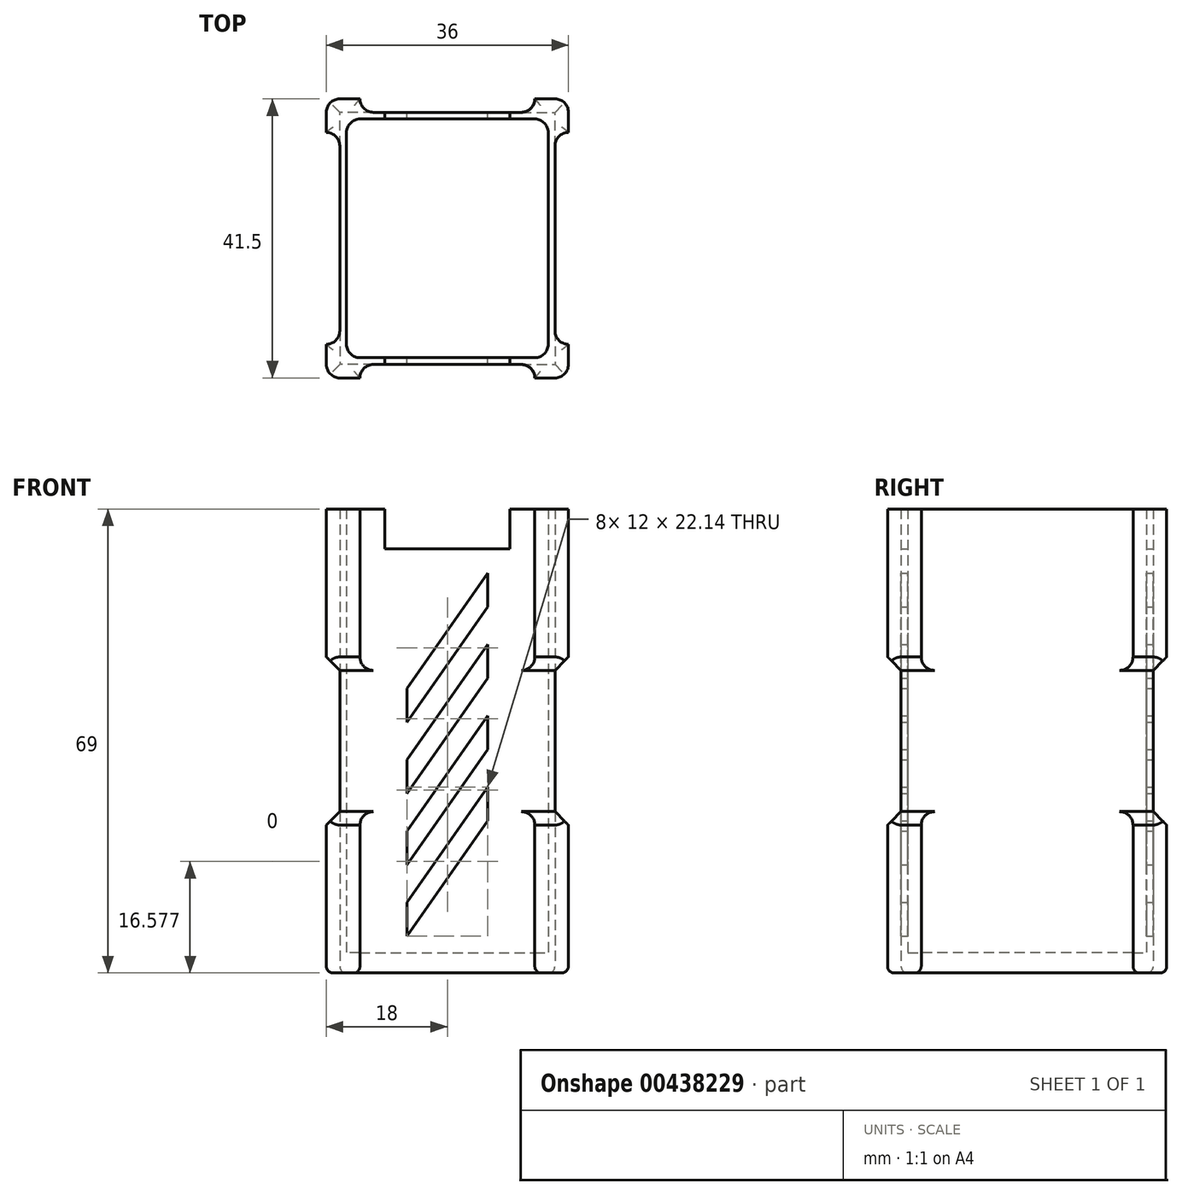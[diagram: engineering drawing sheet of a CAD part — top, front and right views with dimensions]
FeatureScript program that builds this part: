
annotation { "Feature Type Name" : "Feature", "Feature Type Description" : "" }
export const myFeature = defineFeature(function(context is Context, id is Id, definition is map)
    precondition{}
    {
        {
            var Q0;
            Q0=qCreatedBy(makeId("Top.planeOp"),FACE);
            var sketch = newSketch(context, id + "F0", { "sketchPlane" : qUnion([Q0])});
            skLineSegment(sketch, "E0.bottom", {"start": v(-15, 17.75) * mm, "end": v(15, 17.75) * mm});
            skLineSegment(sketch, "E0.top", {"start": v(-15, -17.75) * mm, "end": v(15, -17.75) * mm});
            skLineSegment(sketch, "E0.left", {"start": v(-15, 17.75) * mm, "end": v(-15, -17.75) * mm});
            skLineSegment(sketch, "E0.right", {"start": v(15, 17.75) * mm, "end": v(15, -17.75) * mm});
            skPoint(sketch, "E0.middle", {"position": v(0, 0) * mm});
            skLineSegment(sketch, "E1.0", {"start": v(-16, 18.75) * mm, "end": v(16, 18.75) * mm});
            skLineSegment(sketch, "E1.1", {"start": v(-16, 18.75) * mm, "end": v(-16, -18.75) * mm});
            skLineSegment(sketch, "E1.2", {"start": v(-16, -18.75) * mm, "end": v(16, -18.75) * mm});
            skLineSegment(sketch, "E1.3", {"start": v(16, 18.75) * mm, "end": v(16, -18.75) * mm});
            skLineSegment(sketch, "E2.0", {"start": v(18, 20.75) * mm, "end": v(18, 15.75) * mm});
            skLineSegment(sketch, "E2.1", {"start": v(-18, 20.75) * mm, "end": v(-13, 20.75) * mm});
            skLineSegment(sketch, "E2.2", {"start": v(-18, 20.75) * mm, "end": v(-18, 15.75) * mm});
            skLineSegment(sketch, "E2.3", {"start": v(-18, -20.75) * mm, "end": v(-13, -20.75) * mm});
            skLineSegment(sketch, "E3", {"start": v(-18, 15.75) * mm, "end": v(-16, 15.75) * mm});
            skLineSegment(sketch, "E4", {"start": v(-13, 20.75) * mm, "end": v(-13, 18.75) * mm});
            skLineSegment(sketch, "E5", {"start": v(13, 20.75) * mm, "end": v(13, 18.75) * mm});
            skLineSegment(sketch, "E6", {"start": v(18, -15.75) * mm, "end": v(16, -15.75) * mm});
            skLineSegment(sketch, "E7.trimOffspring", {"start": v(-18, -15.75) * mm, "end": v(-18, -20.75) * mm});
            skLineSegment(sketch, "E8.trimOffspring", {"start": v(13, 20.75) * mm, "end": v(18, 20.75) * mm});
            skLineSegment(sketch, "E9.trimOffspring", {"start": v(18, -15.75) * mm, "end": v(18, -20.75) * mm});
            skLineSegment(sketch, "E10.trimOffspring", {"start": v(13, -20.75) * mm, "end": v(18, -20.75) * mm});
            skLineSegment(sketch, "E11.trimOffspring", {"start": v(16, 15.75) * mm, "end": v(18, 15.75) * mm});
            skLineSegment(sketch, "E12.trimOffspring", {"start": v(-13, -18.75) * mm, "end": v(-13, -20.75) * mm});
            skLineSegment(sketch, "E13.trimOffspring", {"start": v(-16, -15.75) * mm, "end": v(-18, -15.75) * mm});
            skLineSegment(sketch, "E14.trimOffspring", {"start": v(13, -18.75) * mm, "end": v(13, -20.75) * mm});
            skSolve(sketch);
        }
        {
            var Q0;
            Q0 = qSketchRegion(id + "F0", true);
            extrude(context, id + "F1", {"entities" : qUnion([Q0]), "depth" : 66 * mm});
        }
        {
            var Q0;
            Q0=makeQuery(id+"F0.imprint","IMPRINT",FACE,{"disambiguationData":[TD([[makeQuery(id+"F0.imprint","IMPRINT",EDGE,{"derivedFrom":sQuery(id+"F0.wireOp",EDGE,"E0.bottom")}),1.0]])]});
            var Q1;
            Q1=makeQuery(id+"F0.imprint","IMPRINT",FACE,{"disambiguationData":[TD([[makeQuery(id+"F0.imprint","IMPRINT",EDGE,{"derivedFrom":sQuery(id+"F0.wireOp",EDGE,"E0.bottom")}),-1.0]])]});
            var Q2;
            {var subQ3=sQuery(id+"F0.wireOp",EDGE,"E6");Q2=makeQuery(id+"F0.imprint","IMPRINT",FACE,{"disambiguationData":[TD([[makeQuery(id+"F0.imprint","IMPRINT",EDGE,{"derivedFrom":subQ3}),1.0]])]});}
            var Q3;
            Q3=makeQuery(id+"F0.imprint","IMPRINT",FACE,{"disambiguationData":[TD([[makeQuery(id+"F0.imprint","IMPRINT",EDGE,{"derivedFrom":sQuery(id+"F0.wireOp",EDGE,"E2.3")}),1.0]])]});
            var Q4;
            Q4=makeQuery(id+"F0.imprint","IMPRINT",FACE,{"disambiguationData":[TD([[makeQuery(id+"F0.imprint","IMPRINT",EDGE,{"derivedFrom":sQuery(id+"F0.wireOp",EDGE,"E2.0")}),-1.0]])]});
            var Q5;
            Q5=makeQuery(id+"F0.imprint","IMPRINT",FACE,{"disambiguationData":[TD([[makeQuery(id+"F0.imprint","IMPRINT",EDGE,{"derivedFrom":sQuery(id+"F0.wireOp",EDGE,"E2.1")}),-1.0]])]});
            extrude(context, id + "F2", {"entities" : qUnion([Q0, Q1, Q2, Q3, Q4, Q5]), "operationType" : NewBodyOperationType.ADD, "oppositeDirection" : true, "depth" : 3 * mm});
        }
        {
            var Q0;
            {var subQ0=sQuery(id+"F0.wireOp",EDGE,"E13.trimOffspring");var subQ1=sQuery(id+"F0.wireOp",EDGE,"E1.1");Q0=makeQuery(id+"F2.boolean.opBoolean","MERGE",EDGE,{"derivedFrom":[makeQuery(id+"F1.opExtrude","SWEPT_EDGE",EDGE,{"disambiguationData":[OSD([subQ1,subQ0])]}),makeQuery(id+"F2.opExtrude","SWEPT_EDGE",EDGE,{"disambiguationData":[OSD([subQ1,subQ0])]})]});}
            var Q1;
            {var subQ0=sQuery(id+"F0.wireOp",EDGE,"E3");var subQ1=sQuery(id+"F0.wireOp",EDGE,"E1.1");Q1=makeQuery(id+"F2.boolean.opBoolean","MERGE",EDGE,{"derivedFrom":[makeQuery(id+"F1.opExtrude","SWEPT_EDGE",EDGE,{"disambiguationData":[OSD([subQ1,subQ0])]}),makeQuery(id+"F2.opExtrude","SWEPT_EDGE",EDGE,{"disambiguationData":[OSD([subQ1,subQ0])]})]});}
            var Q2;
            {var subQ0=sQuery(id+"F0.wireOp",EDGE,"E4");var subQ1=sQuery(id+"F0.wireOp",EDGE,"E1.0");Q2=makeQuery(id+"F2.boolean.opBoolean","MERGE",EDGE,{"derivedFrom":[makeQuery(id+"F1.opExtrude","SWEPT_EDGE",EDGE,{"disambiguationData":[OSD([subQ1,subQ0])]}),makeQuery(id+"F2.opExtrude","SWEPT_EDGE",EDGE,{"disambiguationData":[OSD([subQ1,subQ0])]})]});}
            var Q3;
            {var subQ0=sQuery(id+"F0.wireOp",EDGE,"E5");var subQ1=sQuery(id+"F0.wireOp",EDGE,"E1.0");Q3=makeQuery(id+"F2.boolean.opBoolean","MERGE",EDGE,{"derivedFrom":[makeQuery(id+"F1.opExtrude","SWEPT_EDGE",EDGE,{"disambiguationData":[OSD([subQ1,subQ0])]}),makeQuery(id+"F2.opExtrude","SWEPT_EDGE",EDGE,{"disambiguationData":[OSD([subQ1,subQ0])]})]});}
            var Q4;
            {var subQ0=sQuery(id+"F0.wireOp",EDGE,"E11.trimOffspring");var subQ1=sQuery(id+"F0.wireOp",EDGE,"E1.3");Q4=makeQuery(id+"F2.boolean.opBoolean","MERGE",EDGE,{"derivedFrom":[makeQuery(id+"F1.opExtrude","SWEPT_EDGE",EDGE,{"disambiguationData":[OSD([subQ1,subQ0])]}),makeQuery(id+"F2.opExtrude","SWEPT_EDGE",EDGE,{"disambiguationData":[OSD([subQ1,subQ0])]})]});}
            var Q5;
            {var subQ0=sQuery(id+"F0.wireOp",EDGE,"E14.trimOffspring");var subQ1=sQuery(id+"F0.wireOp",EDGE,"E1.2");Q5=makeQuery(id+"F2.boolean.opBoolean","MERGE",EDGE,{"derivedFrom":[makeQuery(id+"F1.opExtrude","SWEPT_EDGE",EDGE,{"disambiguationData":[OSD([subQ1,subQ0])]}),makeQuery(id+"F2.opExtrude","SWEPT_EDGE",EDGE,{"disambiguationData":[OSD([subQ1,subQ0])]})]});}
            var Q6;
            {var subQ0=sQuery(id+"F0.wireOp",EDGE,"E6");var subQ1=sQuery(id+"F0.wireOp",EDGE,"E1.3");Q6=makeQuery(id+"F2.boolean.opBoolean","MERGE",EDGE,{"derivedFrom":[makeQuery(id+"F1.opExtrude","SWEPT_EDGE",EDGE,{"disambiguationData":[OSD([subQ1,subQ0])]}),makeQuery(id+"F2.opExtrude","SWEPT_EDGE",EDGE,{"disambiguationData":[OSD([subQ1,subQ0])]})]});}
            var Q7;
            {var subQ0=sQuery(id+"F0.wireOp",EDGE,"E12.trimOffspring");var subQ1=sQuery(id+"F0.wireOp",EDGE,"E1.2");Q7=makeQuery(id+"F2.boolean.opBoolean","MERGE",EDGE,{"derivedFrom":[makeQuery(id+"F1.opExtrude","SWEPT_EDGE",EDGE,{"disambiguationData":[OSD([subQ1,subQ0])]}),makeQuery(id+"F2.opExtrude","SWEPT_EDGE",EDGE,{"disambiguationData":[OSD([subQ1,subQ0])]})]});}
            fillet(context, id + "F3", {"entities" : qUnion([Q0, Q1, Q2, Q3, Q4, Q5, Q6, Q7]), "radius" : 2 * mm, "tangentPropagation" : true, "allowEdgeOverflow" : false});
        }
        {
            var Q0;
            {var subQ0=sQuery(id+"F0.wireOp",EDGE,"E8.trimOffspring");var subQ1=sQuery(id+"F0.wireOp",EDGE,"E2.0");Q0=makeQuery(id+"F2.boolean.opBoolean","MERGE",EDGE,{"derivedFrom":[makeQuery(id+"F1.opExtrude","SWEPT_EDGE",EDGE,{"disambiguationData":[OSD([subQ1,subQ0])]}),makeQuery(id+"F2.opExtrude","SWEPT_EDGE",EDGE,{"disambiguationData":[OSD([subQ1,subQ0])]})]});}
            var Q1;
            {var subQ0=sQuery(id+"F0.wireOp",EDGE,"E7.trimOffspring");var subQ1=sQuery(id+"F0.wireOp",EDGE,"E2.3");Q1=makeQuery(id+"F2.boolean.opBoolean","MERGE",EDGE,{"derivedFrom":[makeQuery(id+"F1.opExtrude","SWEPT_EDGE",EDGE,{"disambiguationData":[OSD([subQ1,subQ0])]}),makeQuery(id+"F2.opExtrude","SWEPT_EDGE",EDGE,{"disambiguationData":[OSD([subQ1,subQ0])]})]});}
            var Q2;
            {var subQ0=sQuery(id+"F0.wireOp",EDGE,"E2.2");var subQ1=sQuery(id+"F0.wireOp",EDGE,"E2.1");Q2=makeQuery(id+"F2.boolean.opBoolean","MERGE",EDGE,{"derivedFrom":[makeQuery(id+"F1.opExtrude","SWEPT_EDGE",EDGE,{"disambiguationData":[OSD([subQ1,subQ0])]}),makeQuery(id+"F2.opExtrude","SWEPT_EDGE",EDGE,{"disambiguationData":[OSD([subQ1,subQ0])]})]});}
            var Q3;
            {var subQ0=sQuery(id+"F0.wireOp",EDGE,"E10.trimOffspring");var subQ1=sQuery(id+"F0.wireOp",EDGE,"E9.trimOffspring");Q3=makeQuery(id+"F2.boolean.opBoolean","MERGE",EDGE,{"derivedFrom":[makeQuery(id+"F1.opExtrude","SWEPT_EDGE",EDGE,{"disambiguationData":[OSD([subQ1,subQ0])]}),makeQuery(id+"F2.opExtrude","SWEPT_EDGE",EDGE,{"disambiguationData":[OSD([subQ1,subQ0])]})]});}
            fillet(context, id + "F4", {"entities" : qUnion([Q0, Q1, Q2, Q3]), "radius" : 2 * mm, "tangentPropagation" : true, "allowEdgeOverflow" : false});
        }
        {
            var Q0;
            Q0=makeQuery(id+"F2.opExtrude","CAP_FACE",FACE,{"disambiguationData":[OSD([sQuery(id+"F0.wireOp",EDGE,"E1.0"),sQuery(id+"F0.wireOp",EDGE,"E1.1"),sQuery(id+"F0.wireOp",EDGE,"E1.2"),sQuery(id+"F0.wireOp",EDGE,"E1.3"),sQuery(id+"F0.wireOp",EDGE,"E2.0"),sQuery(id+"F0.wireOp",EDGE,"E2.1"),sQuery(id+"F0.wireOp",EDGE,"E2.2"),sQuery(id+"F0.wireOp",EDGE,"E2.3"),sQuery(id+"F0.wireOp",EDGE,"E3"),sQuery(id+"F0.wireOp",EDGE,"E4"),sQuery(id+"F0.wireOp",EDGE,"E5"),sQuery(id+"F0.wireOp",EDGE,"E6"),sQuery(id+"F0.wireOp",EDGE,"E7.trimOffspring"),sQuery(id+"F0.wireOp",EDGE,"E8.trimOffspring"),sQuery(id+"F0.wireOp",EDGE,"E9.trimOffspring"),sQuery(id+"F0.wireOp",EDGE,"E10.trimOffspring"),sQuery(id+"F0.wireOp",EDGE,"E11.trimOffspring"),sQuery(id+"F0.wireOp",EDGE,"E12.trimOffspring"),sQuery(id+"F0.wireOp",EDGE,"E13.trimOffspring"),sQuery(id+"F0.wireOp",EDGE,"E14.trimOffspring")])],"isStart":false});
            var Q1;
            Q1=makeQuery(id+"F1.opExtrude","CAP_FACE",FACE,{"disambiguationData":[OSD([sQuery(id+"F0.wireOp",EDGE,"E0.bottom"),sQuery(id+"F0.wireOp",EDGE,"E0.top"),sQuery(id+"F0.wireOp",EDGE,"E0.left"),sQuery(id+"F0.wireOp",EDGE,"E0.right"),sQuery(id+"F0.wireOp",EDGE,"E1.0"),sQuery(id+"F0.wireOp",EDGE,"E1.1"),sQuery(id+"F0.wireOp",EDGE,"E1.2"),sQuery(id+"F0.wireOp",EDGE,"E1.3"),sQuery(id+"F0.wireOp",EDGE,"E2.0"),sQuery(id+"F0.wireOp",EDGE,"E2.1"),sQuery(id+"F0.wireOp",EDGE,"E2.2"),sQuery(id+"F0.wireOp",EDGE,"E2.3"),sQuery(id+"F0.wireOp",EDGE,"E3"),sQuery(id+"F0.wireOp",EDGE,"E4"),sQuery(id+"F0.wireOp",EDGE,"E5"),sQuery(id+"F0.wireOp",EDGE,"E6"),sQuery(id+"F0.wireOp",EDGE,"E7.trimOffspring"),sQuery(id+"F0.wireOp",EDGE,"E8.trimOffspring"),sQuery(id+"F0.wireOp",EDGE,"E9.trimOffspring"),sQuery(id+"F0.wireOp",EDGE,"E10.trimOffspring"),sQuery(id+"F0.wireOp",EDGE,"E11.trimOffspring"),sQuery(id+"F0.wireOp",EDGE,"E12.trimOffspring"),sQuery(id+"F0.wireOp",EDGE,"E13.trimOffspring"),sQuery(id+"F0.wireOp",EDGE,"E14.trimOffspring")])],"isStart":false});
            cPlane(context, id + "F5", {"entities" : qUnion([Q0, Q1]), "cplaneType" : CPlaneType.MID_PLANE, "offset" : 25 * mm, "width" : 150 * mm, "height" : 150 * mm});
        }
        {
            var Q0;
            Q0=qCreatedBy(id+"F5.planeOp",FACE);
            var sketch = newSketch(context, id + "F6", { "sketchPlane" : qUnion([Q0])});
            skLineSegment(sketch, "E15.bottom", {"start": v(18, 20.75) * mm, "end": v(-18, 20.75) * mm});
            skLineSegment(sketch, "E15.top", {"start": v(18, -20.75) * mm, "end": v(-18, -20.75) * mm});
            skLineSegment(sketch, "E15.left", {"start": v(18, 20.75) * mm, "end": v(18, -20.75) * mm});
            skLineSegment(sketch, "E15.right", {"start": v(-18, 20.75) * mm, "end": v(-18, -20.75) * mm});
            skLineSegment(sketch, "E16.0", {"start": v(16, -18.75) * mm, "end": v(-16, -18.75) * mm});
            skLineSegment(sketch, "E16.1", {"start": v(16, 18.75) * mm, "end": v(16, -18.75) * mm});
            skLineSegment(sketch, "E16.2", {"start": v(16, 18.75) * mm, "end": v(-16, 18.75) * mm});
            skLineSegment(sketch, "E16.3", {"start": v(-16, 18.75) * mm, "end": v(-16, -18.75) * mm});
            skSolve(sketch);
        }
        {
            var Q0;
            Q0 = qSketchRegion(id + "F6", true);
            extrude(context, id + "F7", {"entities" : qUnion([Q0]), "operationType" : NewBodyOperationType.REMOVE, "endBound" : BoundingType.SYMMETRIC, "oppositeDirection" : true, "depth" : 25 * mm});
        }
        {
            var Q0;
            {var subQ0=sQuery(id+"F0.wireOp",EDGE,"E1.1");var subQ3=sQuery(id+"F6.wireOp",EDGE,"E16.0");Q0=makeQuery(id+"F7.boolean.opBoolean","COPY",EDGE,{"disambiguationData":[TD([makeQuery(id+"F1.opExtrude","SWEPT_FACE",FACE,{"disambiguationData":[OSD([subQ0])]})])],"derivedFrom":makeQuery(id+"F7.opExtrude","CAP_EDGE",EDGE,{"disambiguationData":[OSD([subQ3])],"isStart":true})});}
            var Q1;
            {var subQ1=sQuery(id+"F0.wireOp",EDGE,"E1.0");var subQ2=sQuery(id+"F6.wireOp",EDGE,"E16.3");Q1=makeQuery(id+"F7.boolean.opBoolean","COPY",EDGE,{"disambiguationData":[TD([makeQuery(id+"F1.opExtrude","SWEPT_FACE",FACE,{"disambiguationData":[OSD([subQ1])]})])],"derivedFrom":makeQuery(id+"F7.opExtrude","CAP_EDGE",EDGE,{"disambiguationData":[OSD([subQ2])],"isStart":true})});}
            var Q2;
            {var subQ0=sQuery(id+"F0.wireOp",EDGE,"E1.3");var subQ3=sQuery(id+"F6.wireOp",EDGE,"E16.0");Q2=makeQuery(id+"F7.boolean.opBoolean","COPY",EDGE,{"disambiguationData":[TD([makeQuery(id+"F1.opExtrude","SWEPT_FACE",FACE,{"disambiguationData":[OSD([subQ0])]})])],"derivedFrom":makeQuery(id+"F7.opExtrude","CAP_EDGE",EDGE,{"disambiguationData":[OSD([subQ3])],"isStart":true})});}
            var Q3;
            {var subQ1=sQuery(id+"F0.wireOp",EDGE,"E1.0");var subQ2=sQuery(id+"F6.wireOp",EDGE,"E16.1");Q3=makeQuery(id+"F7.boolean.opBoolean","COPY",EDGE,{"disambiguationData":[TD([makeQuery(id+"F1.opExtrude","SWEPT_FACE",FACE,{"disambiguationData":[OSD([subQ1])]})])],"derivedFrom":makeQuery(id+"F7.opExtrude","CAP_EDGE",EDGE,{"disambiguationData":[OSD([subQ2])],"isStart":true})});}
            var Q4;
            {var subQ0=sQuery(id+"F0.wireOp",EDGE,"E1.1");var subQ3=sQuery(id+"F6.wireOp",EDGE,"E16.0");Q4=makeQuery(id+"F7.boolean.opBoolean","COPY",EDGE,{"disambiguationData":[TD([makeQuery(id+"F1.opExtrude","SWEPT_FACE",FACE,{"disambiguationData":[OSD([subQ0])]})])],"derivedFrom":makeQuery(id+"F7.opExtrude","CAP_EDGE",EDGE,{"disambiguationData":[OSD([subQ3])],"isStart":false})});}
            var Q5;
            {var subQ1=sQuery(id+"F0.wireOp",EDGE,"E1.0");var subQ2=sQuery(id+"F6.wireOp",EDGE,"E16.3");Q5=makeQuery(id+"F7.boolean.opBoolean","COPY",EDGE,{"disambiguationData":[TD([makeQuery(id+"F1.opExtrude","SWEPT_FACE",FACE,{"disambiguationData":[OSD([subQ1])]})])],"derivedFrom":makeQuery(id+"F7.opExtrude","CAP_EDGE",EDGE,{"disambiguationData":[OSD([subQ2])],"isStart":false})});}
            var Q6;
            {var subQ0=sQuery(id+"F0.wireOp",EDGE,"E1.3");var subQ2=sQuery(id+"F6.wireOp",EDGE,"E16.2");Q6=makeQuery(id+"F7.boolean.opBoolean","COPY",EDGE,{"disambiguationData":[TD([makeQuery(id+"F1.opExtrude","SWEPT_FACE",FACE,{"disambiguationData":[OSD([subQ0])]})])],"derivedFrom":makeQuery(id+"F7.opExtrude","CAP_EDGE",EDGE,{"disambiguationData":[OSD([subQ2])],"isStart":false})});}
            var Q7;
            {var subQ0=sQuery(id+"F0.wireOp",EDGE,"E1.3");var subQ3=sQuery(id+"F6.wireOp",EDGE,"E16.0");Q7=makeQuery(id+"F7.boolean.opBoolean","COPY",EDGE,{"disambiguationData":[TD([makeQuery(id+"F1.opExtrude","SWEPT_FACE",FACE,{"disambiguationData":[OSD([subQ0])]})])],"derivedFrom":makeQuery(id+"F7.opExtrude","CAP_EDGE",EDGE,{"disambiguationData":[OSD([subQ3])],"isStart":false})});}
            var Q8;
            {var subQ1=sQuery(id+"F0.wireOp",EDGE,"E1.2");var subQ3=sQuery(id+"F6.wireOp",EDGE,"E16.1");Q8=makeQuery(id+"F7.boolean.opBoolean","COPY",EDGE,{"disambiguationData":[TD([makeQuery(id+"F1.opExtrude","SWEPT_FACE",FACE,{"disambiguationData":[OSD([subQ1])]})])],"derivedFrom":makeQuery(id+"F7.opExtrude","CAP_EDGE",EDGE,{"disambiguationData":[OSD([subQ3])],"isStart":true})});}
            var Q9;
            {var subQ1=sQuery(id+"F0.wireOp",EDGE,"E1.0");var subQ2=sQuery(id+"F6.wireOp",EDGE,"E16.1");Q9=makeQuery(id+"F7.boolean.opBoolean","COPY",EDGE,{"disambiguationData":[TD([makeQuery(id+"F1.opExtrude","SWEPT_FACE",FACE,{"disambiguationData":[OSD([subQ1])]})])],"derivedFrom":makeQuery(id+"F7.opExtrude","CAP_EDGE",EDGE,{"disambiguationData":[OSD([subQ2])],"isStart":false})});}
            var Q10;
            {var subQ1=sQuery(id+"F0.wireOp",EDGE,"E1.2");var subQ3=sQuery(id+"F6.wireOp",EDGE,"E16.1");Q10=makeQuery(id+"F7.boolean.opBoolean","COPY",EDGE,{"disambiguationData":[TD([makeQuery(id+"F1.opExtrude","SWEPT_FACE",FACE,{"disambiguationData":[OSD([subQ1])]})])],"derivedFrom":makeQuery(id+"F7.opExtrude","CAP_EDGE",EDGE,{"disambiguationData":[OSD([subQ3])],"isStart":false})});}
            var Q11;
            {var subQ2=sQuery(id+"F0.wireOp",EDGE,"E1.1");var subQ3=sQuery(id+"F6.wireOp",EDGE,"E16.2");Q11=makeQuery(id+"F7.boolean.opBoolean","COPY",EDGE,{"disambiguationData":[TD([makeQuery(id+"F1.opExtrude","SWEPT_FACE",FACE,{"disambiguationData":[OSD([subQ2])]})])],"derivedFrom":makeQuery(id+"F7.opExtrude","CAP_EDGE",EDGE,{"disambiguationData":[OSD([subQ3])],"isStart":false})});}
            var Q12;
            {var subQ0=sQuery(id+"F0.wireOp",EDGE,"E1.2");var subQ1=sQuery(id+"F6.wireOp",EDGE,"E16.3");Q12=makeQuery(id+"F7.boolean.opBoolean","COPY",EDGE,{"disambiguationData":[TD([makeQuery(id+"F1.opExtrude","SWEPT_FACE",FACE,{"disambiguationData":[OSD([subQ0])]})])],"derivedFrom":makeQuery(id+"F7.opExtrude","CAP_EDGE",EDGE,{"disambiguationData":[OSD([subQ1])],"isStart":false})});}
            var Q13;
            {var subQ0=sQuery(id+"F0.wireOp",EDGE,"E1.2");var subQ1=sQuery(id+"F6.wireOp",EDGE,"E16.3");Q13=makeQuery(id+"F7.boolean.opBoolean","COPY",EDGE,{"disambiguationData":[TD([makeQuery(id+"F1.opExtrude","SWEPT_FACE",FACE,{"disambiguationData":[OSD([subQ0])]})])],"derivedFrom":makeQuery(id+"F7.opExtrude","CAP_EDGE",EDGE,{"disambiguationData":[OSD([subQ1])],"isStart":true})});}
            var Q14;
            {var subQ2=sQuery(id+"F0.wireOp",EDGE,"E1.1");var subQ3=sQuery(id+"F6.wireOp",EDGE,"E16.2");Q14=makeQuery(id+"F7.boolean.opBoolean","COPY",EDGE,{"disambiguationData":[TD([makeQuery(id+"F1.opExtrude","SWEPT_FACE",FACE,{"disambiguationData":[OSD([subQ2])]})])],"derivedFrom":makeQuery(id+"F7.opExtrude","CAP_EDGE",EDGE,{"disambiguationData":[OSD([subQ3])],"isStart":true})});}
            var Q15;
            {var subQ0=sQuery(id+"F0.wireOp",EDGE,"E1.3");var subQ2=sQuery(id+"F6.wireOp",EDGE,"E16.2");Q15=makeQuery(id+"F7.boolean.opBoolean","COPY",EDGE,{"disambiguationData":[TD([makeQuery(id+"F1.opExtrude","SWEPT_FACE",FACE,{"disambiguationData":[OSD([subQ0])]})])],"derivedFrom":makeQuery(id+"F7.opExtrude","CAP_EDGE",EDGE,{"disambiguationData":[OSD([subQ2])],"isStart":true})});}
            chamfer(context, id + "F8", {"entities" : qUnion([Q0, Q1, Q2, Q3, Q4, Q5, Q6, Q7, Q8, Q9, Q10, Q11, Q12, Q13, Q14, Q15]), "chamferType" : ChamferType.OFFSET_ANGLE, "width" : 2 * mm, "oppositeDirection" : false, "angle" : 45 * degree, "tangentPropagation" : true});
        }
        {
            var Q0;
            Q0=makeQuery(id+"F2.opExtrude","CAP_EDGE",EDGE,{"disambiguationData":[OSD([sQuery(id+"F0.wireOp",EDGE,"E2.2")])],"isStart":false});
            var Q1;
            Q1=makeQuery(id+"F2.opExtrude","CAP_EDGE",EDGE,{"disambiguationData":[OSD([sQuery(id+"F0.wireOp",EDGE,"E1.1")])],"isStart":false});
            var Q2;
            {var subQ0=sQuery(id+"F0.wireOp",EDGE,"E7.trimOffspring");var subQ1=sQuery(id+"F0.wireOp",EDGE,"E2.3");Q2=makeQuery(id+"F4.opFillet","BLEND_EDGE",EDGE,{"blendedFrom":[makeQuery(id+"F2.boolean.opBoolean","MERGE",EDGE,{"derivedFrom":[makeQuery(id+"F1.opExtrude","SWEPT_EDGE",EDGE,{"disambiguationData":[OSD([subQ1,subQ0])]}),makeQuery(id+"F2.opExtrude","SWEPT_EDGE",EDGE,{"disambiguationData":[OSD([subQ1,subQ0])]})]}),makeQuery(id+"F2.opExtrude","CAP_FACE",FACE,{"disambiguationData":[OSD([sQuery(id+"F0.wireOp",EDGE,"E1.0"),sQuery(id+"F0.wireOp",EDGE,"E1.1"),sQuery(id+"F0.wireOp",EDGE,"E1.2"),sQuery(id+"F0.wireOp",EDGE,"E1.3"),sQuery(id+"F0.wireOp",EDGE,"E2.0"),sQuery(id+"F0.wireOp",EDGE,"E2.1"),sQuery(id+"F0.wireOp",EDGE,"E2.2"),subQ1,sQuery(id+"F0.wireOp",EDGE,"E3"),sQuery(id+"F0.wireOp",EDGE,"E4"),sQuery(id+"F0.wireOp",EDGE,"E5"),sQuery(id+"F0.wireOp",EDGE,"E6"),subQ0,sQuery(id+"F0.wireOp",EDGE,"E8.trimOffspring"),sQuery(id+"F0.wireOp",EDGE,"E9.trimOffspring"),sQuery(id+"F0.wireOp",EDGE,"E10.trimOffspring"),sQuery(id+"F0.wireOp",EDGE,"E11.trimOffspring"),sQuery(id+"F0.wireOp",EDGE,"E12.trimOffspring"),sQuery(id+"F0.wireOp",EDGE,"E13.trimOffspring"),sQuery(id+"F0.wireOp",EDGE,"E14.trimOffspring")])],"isStart":false})],"blendedInto":[makeQuery(id+"F2.opExtrude","CAP_FACE",FACE,{"disambiguationData":[OSD([sQuery(id+"F0.wireOp",EDGE,"E1.0"),sQuery(id+"F0.wireOp",EDGE,"E1.1"),sQuery(id+"F0.wireOp",EDGE,"E1.2"),sQuery(id+"F0.wireOp",EDGE,"E1.3"),sQuery(id+"F0.wireOp",EDGE,"E2.0"),sQuery(id+"F0.wireOp",EDGE,"E2.1"),sQuery(id+"F0.wireOp",EDGE,"E2.2"),subQ1,sQuery(id+"F0.wireOp",EDGE,"E3"),sQuery(id+"F0.wireOp",EDGE,"E4"),sQuery(id+"F0.wireOp",EDGE,"E5"),sQuery(id+"F0.wireOp",EDGE,"E6"),subQ0,sQuery(id+"F0.wireOp",EDGE,"E8.trimOffspring"),sQuery(id+"F0.wireOp",EDGE,"E9.trimOffspring"),sQuery(id+"F0.wireOp",EDGE,"E10.trimOffspring"),sQuery(id+"F0.wireOp",EDGE,"E11.trimOffspring"),sQuery(id+"F0.wireOp",EDGE,"E12.trimOffspring"),sQuery(id+"F0.wireOp",EDGE,"E13.trimOffspring"),sQuery(id+"F0.wireOp",EDGE,"E14.trimOffspring")])],"isStart":false})]});}
            var Q3;
            Q3=makeQuery(id+"F2.opExtrude","CAP_EDGE",EDGE,{"disambiguationData":[OSD([sQuery(id+"F0.wireOp",EDGE,"E1.2")])],"isStart":false});
            var Q4;
            Q4=makeQuery(id+"F2.opExtrude","CAP_EDGE",EDGE,{"disambiguationData":[OSD([sQuery(id+"F0.wireOp",EDGE,"E2.0")])],"isStart":false});
            var Q5;
            Q5=makeQuery(id+"F2.opExtrude","CAP_EDGE",EDGE,{"disambiguationData":[OSD([sQuery(id+"F0.wireOp",EDGE,"E1.3")])],"isStart":false});
            var Q6;
            Q6=makeQuery(id+"F2.opExtrude","CAP_EDGE",EDGE,{"disambiguationData":[OSD([sQuery(id+"F0.wireOp",EDGE,"E1.0")])],"isStart":false});
            var Q7;
            {var subQ0=sQuery(id+"F0.wireOp",EDGE,"E10.trimOffspring");var subQ1=sQuery(id+"F0.wireOp",EDGE,"E9.trimOffspring");Q7=makeQuery(id+"F4.opFillet","BLEND_EDGE",EDGE,{"blendedFrom":[makeQuery(id+"F2.boolean.opBoolean","MERGE",EDGE,{"derivedFrom":[makeQuery(id+"F1.opExtrude","SWEPT_EDGE",EDGE,{"disambiguationData":[OSD([subQ1,subQ0])]}),makeQuery(id+"F2.opExtrude","SWEPT_EDGE",EDGE,{"disambiguationData":[OSD([subQ1,subQ0])]})]}),makeQuery(id+"F2.opExtrude","CAP_FACE",FACE,{"disambiguationData":[OSD([sQuery(id+"F0.wireOp",EDGE,"E1.0"),sQuery(id+"F0.wireOp",EDGE,"E1.1"),sQuery(id+"F0.wireOp",EDGE,"E1.2"),sQuery(id+"F0.wireOp",EDGE,"E1.3"),sQuery(id+"F0.wireOp",EDGE,"E2.0"),sQuery(id+"F0.wireOp",EDGE,"E2.1"),sQuery(id+"F0.wireOp",EDGE,"E2.2"),sQuery(id+"F0.wireOp",EDGE,"E2.3"),sQuery(id+"F0.wireOp",EDGE,"E3"),sQuery(id+"F0.wireOp",EDGE,"E4"),sQuery(id+"F0.wireOp",EDGE,"E5"),sQuery(id+"F0.wireOp",EDGE,"E6"),sQuery(id+"F0.wireOp",EDGE,"E7.trimOffspring"),sQuery(id+"F0.wireOp",EDGE,"E8.trimOffspring"),subQ1,subQ0,sQuery(id+"F0.wireOp",EDGE,"E11.trimOffspring"),sQuery(id+"F0.wireOp",EDGE,"E12.trimOffspring"),sQuery(id+"F0.wireOp",EDGE,"E13.trimOffspring"),sQuery(id+"F0.wireOp",EDGE,"E14.trimOffspring")])],"isStart":false})],"blendedInto":[makeQuery(id+"F2.opExtrude","CAP_FACE",FACE,{"disambiguationData":[OSD([sQuery(id+"F0.wireOp",EDGE,"E1.0"),sQuery(id+"F0.wireOp",EDGE,"E1.1"),sQuery(id+"F0.wireOp",EDGE,"E1.2"),sQuery(id+"F0.wireOp",EDGE,"E1.3"),sQuery(id+"F0.wireOp",EDGE,"E2.0"),sQuery(id+"F0.wireOp",EDGE,"E2.1"),sQuery(id+"F0.wireOp",EDGE,"E2.2"),sQuery(id+"F0.wireOp",EDGE,"E2.3"),sQuery(id+"F0.wireOp",EDGE,"E3"),sQuery(id+"F0.wireOp",EDGE,"E4"),sQuery(id+"F0.wireOp",EDGE,"E5"),sQuery(id+"F0.wireOp",EDGE,"E6"),sQuery(id+"F0.wireOp",EDGE,"E7.trimOffspring"),sQuery(id+"F0.wireOp",EDGE,"E8.trimOffspring"),subQ1,subQ0,sQuery(id+"F0.wireOp",EDGE,"E11.trimOffspring"),sQuery(id+"F0.wireOp",EDGE,"E12.trimOffspring"),sQuery(id+"F0.wireOp",EDGE,"E13.trimOffspring"),sQuery(id+"F0.wireOp",EDGE,"E14.trimOffspring")])],"isStart":false})]});}
            fillet(context, id + "F9", {"entities" : qUnion([Q0, Q1, Q2, Q3, Q4, Q5, Q6, Q7]), "radius" : 1 * mm, "tangentPropagation" : true, "allowEdgeOverflow" : false});
        }
        {
            var Q0;
            Q0=makeQuery(id+"F1.opExtrude","CAP_EDGE",EDGE,{"disambiguationData":[OSD([sQuery(id+"F0.wireOp",EDGE,"E0.left")])],"isStart":true});
            var Q1;
            Q1=makeQuery(id+"F1.opExtrude","CAP_EDGE",EDGE,{"disambiguationData":[OSD([sQuery(id+"F0.wireOp",EDGE,"E0.top")])],"isStart":true});
            var Q2;
            Q2=makeQuery(id+"F1.opExtrude","CAP_EDGE",EDGE,{"disambiguationData":[OSD([sQuery(id+"F0.wireOp",EDGE,"E0.right")])],"isStart":true});
            var Q3;
            Q3=makeQuery(id+"F1.opExtrude","CAP_EDGE",EDGE,{"disambiguationData":[OSD([sQuery(id+"F0.wireOp",EDGE,"E0.bottom")])],"isStart":true});
            var Q4;
            Q4=makeQuery(id+"F1.opExtrude","SWEPT_EDGE",EDGE,{"disambiguationData":[OSD([sQuery(id+"F0.wireOp",EDGE,"E0.bottom"),sQuery(id+"F0.wireOp",EDGE,"E0.left")])]});
            var Q5;
            Q5=makeQuery(id+"F1.opExtrude","SWEPT_EDGE",EDGE,{"disambiguationData":[OSD([sQuery(id+"F0.wireOp",EDGE,"E0.bottom"),sQuery(id+"F0.wireOp",EDGE,"E0.right")])]});
            var Q6;
            Q6=makeQuery(id+"F1.opExtrude","SWEPT_EDGE",EDGE,{"disambiguationData":[OSD([sQuery(id+"F0.wireOp",EDGE,"E0.top"),sQuery(id+"F0.wireOp",EDGE,"E0.left")])]});
            var Q7;
            Q7=makeQuery(id+"F1.opExtrude","SWEPT_EDGE",EDGE,{"disambiguationData":[OSD([sQuery(id+"F0.wireOp",EDGE,"E0.top"),sQuery(id+"F0.wireOp",EDGE,"E0.right")])]});
            fillet(context, id + "F10", {"entities" : qUnion([Q0, Q1, Q2, Q3, Q4, Q5, Q6, Q7]), "radius" : 2 * mm, "tangentPropagation" : true, "allowEdgeOverflow" : false});
        }
        {
            var Q0;
            {var subQ0=sQuery(id+"F0.wireOp",EDGE,"E1.0");Q0=makeQuery(id+"F7.boolean.opBoolean","MERGE",FACE,{"derivedFrom":[makeQuery(id+"F2.boolean.opBoolean","MERGE",FACE,{"derivedFrom":[makeQuery(id+"F1.opExtrude","SWEPT_FACE",FACE,{"disambiguationData":[OSD([subQ0])]}),makeQuery(id+"F2.opExtrude","SWEPT_FACE",FACE,{"disambiguationData":[OSD([subQ0])]})]}),makeQuery(id+"F7.opExtrude","SWEPT_FACE",FACE,{"disambiguationData":[OSD([sQuery(id+"F6.wireOp",EDGE,"E16.0")])]})]});}
            var sketch = newSketch(context, id + "F11", { "sketchPlane" : qUnion([Q0])});
            skLineSegment(sketch, "E17.bottom", {"start": v(-9.3, 71.94) * mm, "end": v(9.3, 71.94) * mm});
            skLineSegment(sketch, "E17.top", {"start": v(-9.3, 60.06) * mm, "end": v(9.3, 60.06) * mm});
            skLineSegment(sketch, "E17.left", {"start": v(-9.3, 71.94) * mm, "end": v(-9.3, 60.06) * mm});
            skLineSegment(sketch, "E17.right", {"start": v(9.3, 71.94) * mm, "end": v(9.3, 60.06) * mm});
            skPoint(sketch, "E17.middle", {"position": v(0, 66) * mm});
            skLineSegment(sketch, "E18", {"start": v(6, 2.5) * mm, "end": v(-6, 19.65) * mm});
            skLineSegment(sketch, "E19", {"start": v(-6, 19.65) * mm, "end": v(-6, 24.65) * mm});
            skLineSegment(sketch, "E20", {"start": v(-6, 24.65) * mm, "end": v(6, 7.5) * mm});
            skLineSegment(sketch, "E21", {"start": v(6, 7.5) * mm, "end": v(6, 2.5) * mm});
            skLineSegment(sketch, "E22.0.1.0", {"start": v(6, 13.1) * mm, "end": v(-6, 30.25) * mm});
            skLineSegment(sketch, "E22.0.1.1", {"start": v(-6, 30.25) * mm, "end": v(-6, 35.25) * mm});
            skLineSegment(sketch, "E22.0.1.2", {"start": v(-6, 35.25) * mm, "end": v(6, 18.1) * mm});
            skLineSegment(sketch, "E22.0.1.3", {"start": v(6, 18.1) * mm, "end": v(6, 13.1) * mm});
            skLineSegment(sketch, "E22.0.2.0", {"start": v(6, 23.7) * mm, "end": v(-6, 40.85) * mm});
            skLineSegment(sketch, "E22.0.2.1", {"start": v(-6, 40.85) * mm, "end": v(-6, 45.85) * mm});
            skLineSegment(sketch, "E22.0.2.2", {"start": v(-6, 45.85) * mm, "end": v(6, 28.7) * mm});
            skLineSegment(sketch, "E22.0.2.3", {"start": v(6, 28.7) * mm, "end": v(6, 23.7) * mm});
            skLineSegment(sketch, "E22.0.3.0", {"start": v(6, 34.3) * mm, "end": v(-6, 51.45) * mm});
            skLineSegment(sketch, "E22.0.3.1", {"start": v(-6, 51.45) * mm, "end": v(-6, 56.45) * mm});
            skLineSegment(sketch, "E22.0.3.2", {"start": v(-6, 56.45) * mm, "end": v(6, 39.3) * mm});
            skLineSegment(sketch, "E22.0.3.3", {"start": v(6, 39.3) * mm, "end": v(6, 34.3) * mm});
            skLineSegment(sketch, "E22.direction1", {"start": v(6, 2.5) * mm, "end": v(32, 2.5) * mm, "construction": true});
            skLineSegment(sketch, "E22.direction2", {"start": v(6, 2.5) * mm, "end": v(6, 13.1) * mm, "construction": true});
            skSolve(sketch);
        }
        {
            var Q0;
            Q0 = qSketchRegion(id + "F11", true);
            extrude(context, id + "F12", {"entities" : qUnion([Q0]), "operationType" : NewBodyOperationType.REMOVE, "endBound" : BoundingType.THROUGH_ALL, "oppositeDirection" : true, "depth" : 25 * mm});
        }
    });
